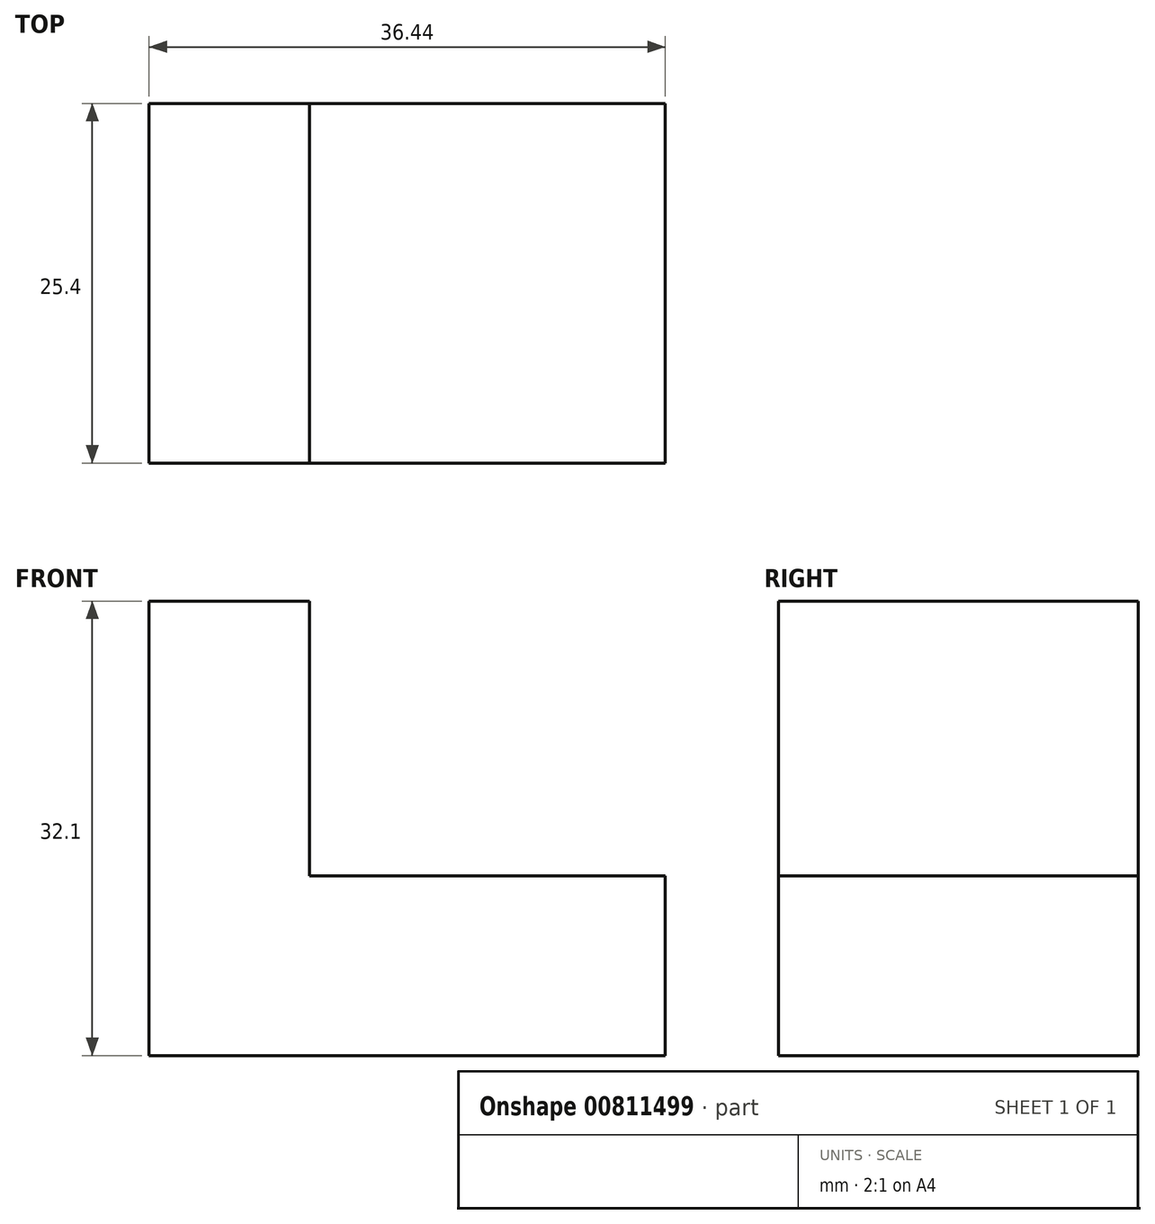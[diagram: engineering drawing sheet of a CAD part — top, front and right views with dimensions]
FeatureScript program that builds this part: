
annotation { "Feature Type Name" : "Feature", "Feature Type Description" : "" }
export const myFeature = defineFeature(function(context is Context, id is Id, definition is map)
    precondition{}
    {
        {
            var Q0;
            Q0=qCreatedBy(makeId("Front.planeOp"),FACE);
            var sketch = newSketch(context, id + "F0", { "sketchPlane" : qUnion([Q0])});
            skLineSegment(sketch, "E0", {"start": v(0, 0) * mm, "end": v(0, 32.1) * mm});
            skLineSegment(sketch, "E1", {"start": v(0, 32.1) * mm, "end": v(11.32, 32.1) * mm});
            skLineSegment(sketch, "E2", {"start": v(11.32, 32.1) * mm, "end": v(11.32, 12.7) * mm});
            skLineSegment(sketch, "E3", {"start": v(11.32, 12.7) * mm, "end": v(36.44, 12.7) * mm});
            skLineSegment(sketch, "E4", {"start": v(36.44, 12.7) * mm, "end": v(36.44, 0) * mm});
            skLineSegment(sketch, "E5", {"start": v(36.44, 0) * mm, "end": v(0, 0) * mm});
            skSolve(sketch);
        }
        {
            var Q0;
            Q0 = qSketchRegion(id + "F0", true);
            extrude(context, id + "F1", {"entities" : qUnion([Q0]), "depth" : 25.4 * mm, "offsetDistance" : 25.4 * mm});
        }
    });
